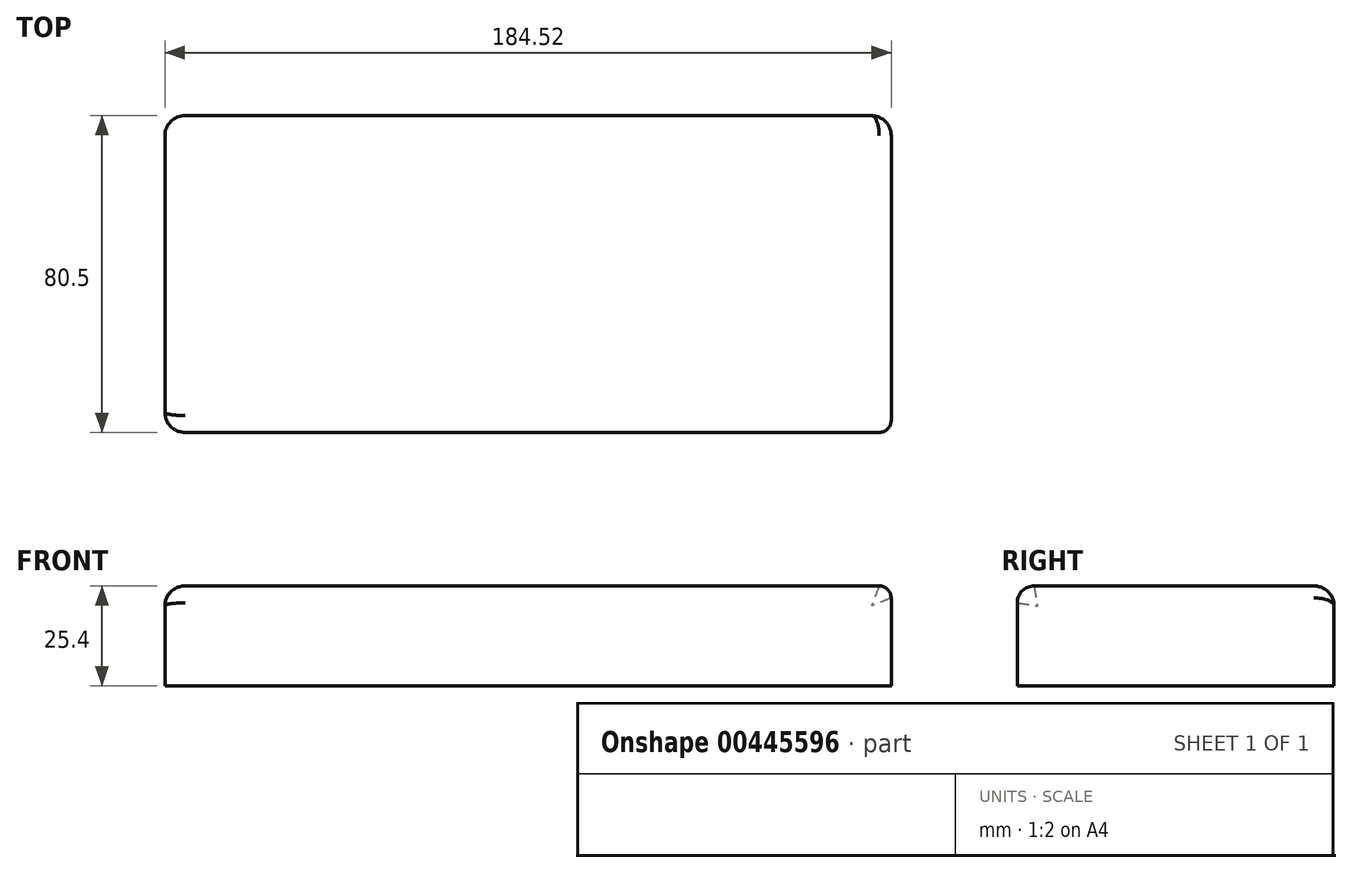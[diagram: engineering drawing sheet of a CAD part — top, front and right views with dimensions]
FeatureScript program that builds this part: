
annotation { "Feature Type Name" : "Feature", "Feature Type Description" : "" }
export const myFeature = defineFeature(function(context is Context, id is Id, definition is map)
    precondition{}
    {
        {
            var Q0;
            Q0=qCreatedBy(makeId("Top.planeOp"),FACE);
            var sketch = newSketch(context, id + "F0", { "sketchPlane" : qUnion([Q0])});
            skLineSegment(sketch, "E0.bottom", {"start": v(-92.26, 40.25) * mm, "end": v(92.26, 40.25) * mm});
            skLineSegment(sketch, "E0.top", {"start": v(-92.26, -40.25) * mm, "end": v(92.26, -40.25) * mm});
            skLineSegment(sketch, "E0.left", {"start": v(-92.26, 40.25) * mm, "end": v(-92.26, -40.25) * mm});
            skLineSegment(sketch, "E0.right", {"start": v(92.26, 40.25) * mm, "end": v(92.26, -40.25) * mm});
            skPoint(sketch, "E0.middle", {"position": v(0, 0) * mm});
            skSolve(sketch);
        }
        {
            var Q0;
            Q0=makeQuery(id+"F0.imprint","IMPRINT",FACE,{"disambiguationData":[TD([[makeQuery(id+"F0.imprint","IMPRINT",EDGE,{"derivedFrom":sQuery(id+"F0.wireOp",EDGE,"E0.bottom")}),-1.0]])]});
            extrude(context, id + "F1", {"entities" : qUnion([Q0]), "depth" : 25.4 * mm});
        }
        {
            var Q0;
            Q0=makeQuery(id+"F1.opExtrude","CAP_EDGE",EDGE,{"disambiguationData":[OSD([sQuery(id+"F0.wireOp",EDGE,"E0.top")])],"isStart":false});
            fillet(context, id + "F2", {"entities" : qUnion([Q0]), "radius" : 4.3 * mm, "tangentPropagation" : true, "allowEdgeOverflow" : false});
        }
        {
            var Q0;
            Q0=makeQuery(id+"F1.opExtrude","CAP_EDGE",EDGE,{"disambiguationData":[OSD([sQuery(id+"F0.wireOp",EDGE,"E0.right")])],"isStart":false});
            fillet(context, id + "F3", {"entities" : qUnion([Q0]), "radius" : 3.07 * mm, "tangentPropagation" : true, "allowEdgeOverflow" : false});
        }
        {
            var Q0;
            {var subQ0=sQuery(id+"F0.wireOp",EDGE,"E0.right");Q0=makeQuery(id+"F3.opFillet","BLEND_EDGE",EDGE,{"blendedFrom":[makeQuery(id+"F1.opExtrude","CAP_EDGE",EDGE,{"disambiguationData":[OSD([subQ0])],"isStart":false}),makeQuery(id+"F1.opExtrude","CAP_FACE",FACE,{"disambiguationData":[OSD([sQuery(id+"F0.wireOp",EDGE,"E0.bottom"),sQuery(id+"F0.wireOp",EDGE,"E0.top"),sQuery(id+"F0.wireOp",EDGE,"E0.left"),subQ0])],"isStart":false})],"blendedInto":[makeQuery(id+"F1.opExtrude","CAP_FACE",FACE,{"disambiguationData":[OSD([sQuery(id+"F0.wireOp",EDGE,"E0.bottom"),sQuery(id+"F0.wireOp",EDGE,"E0.top"),sQuery(id+"F0.wireOp",EDGE,"E0.left"),subQ0])],"isStart":false})]});}
            var Q1;
            Q1=makeQuery(id+"F1.opExtrude","SWEPT_EDGE",EDGE,{"disambiguationData":[OSD([sQuery(id+"F0.wireOp",EDGE,"E0.bottom"),sQuery(id+"F0.wireOp",EDGE,"E0.right")])]});
            var Q2;
            {var subQ0=sQuery(id+"F0.wireOp",EDGE,"E0.top");Q2=makeQuery(id+"F2.opFillet","BLEND_EDGE",EDGE,{"blendedFrom":[makeQuery(id+"F1.opExtrude","CAP_EDGE",EDGE,{"disambiguationData":[OSD([subQ0])],"isStart":false}),makeQuery(id+"F1.opExtrude","CAP_FACE",FACE,{"disambiguationData":[OSD([sQuery(id+"F0.wireOp",EDGE,"E0.bottom"),subQ0,sQuery(id+"F0.wireOp",EDGE,"E0.left"),sQuery(id+"F0.wireOp",EDGE,"E0.right")])],"isStart":false})],"blendedInto":[makeQuery(id+"F1.opExtrude","CAP_FACE",FACE,{"disambiguationData":[OSD([sQuery(id+"F0.wireOp",EDGE,"E0.bottom"),subQ0,sQuery(id+"F0.wireOp",EDGE,"E0.left"),sQuery(id+"F0.wireOp",EDGE,"E0.right")])],"isStart":false})]});}
            var Q3;
            Q3=makeQuery(id+"F1.opExtrude","CAP_EDGE",EDGE,{"disambiguationData":[OSD([sQuery(id+"F0.wireOp",EDGE,"E0.left")])],"isStart":false});
            var Q4;
            Q4=makeQuery(id+"F1.opExtrude","SWEPT_EDGE",EDGE,{"disambiguationData":[OSD([sQuery(id+"F0.wireOp",EDGE,"E0.top"),sQuery(id+"F0.wireOp",EDGE,"E0.left")])]});
            var Q5;
            Q5=makeQuery(id+"F1.opExtrude","SWEPT_EDGE",EDGE,{"disambiguationData":[OSD([sQuery(id+"F0.wireOp",EDGE,"E0.bottom"),sQuery(id+"F0.wireOp",EDGE,"E0.left")])]});
            var Q6;
            Q6=makeQuery(id+"F1.opExtrude","CAP_EDGE",EDGE,{"disambiguationData":[OSD([sQuery(id+"F0.wireOp",EDGE,"E0.bottom")])],"isStart":false});
            fillet(context, id + "F4", {"entities" : qUnion([Q0, Q1, Q2, Q3, Q4, Q5, Q6]), "radius" : 5.08 * mm, "tangentPropagation" : true, "allowEdgeOverflow" : false});
        }
    });
